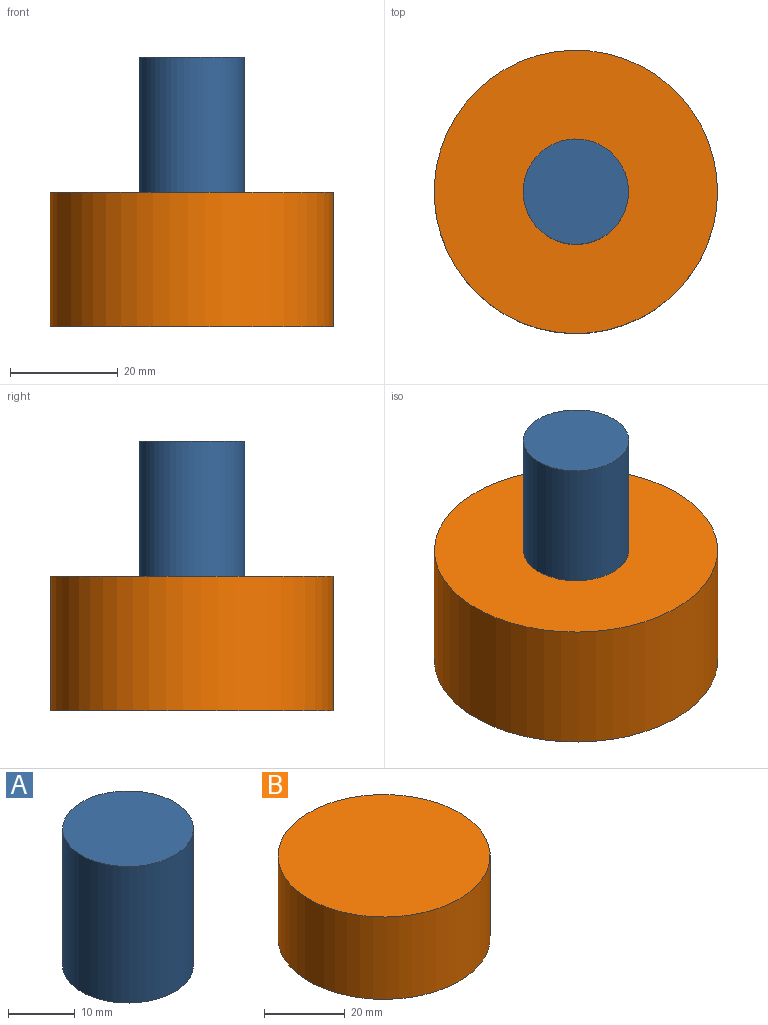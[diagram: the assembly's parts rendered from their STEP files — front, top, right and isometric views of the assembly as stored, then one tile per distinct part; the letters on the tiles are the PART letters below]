
ASSEMBLY  parts=2 mates=1
PART A: 3 faces, bbox 19.6x19.6x25 mm
  f0: cylinder r=9.79mm len=25mm, axis (0,0,-1), area 1537.3mm2, adj f1,f2
  f1: plane 19.57x19.57mm, normal (0,0,1), area 300.9mm2, adj f0
  f2: plane 19.57x19.57mm, normal (0,0,-1), area 300.9mm2, adj f0
PART B: 3 faces, bbox 52.6x52.6x25 mm
  f0: cylinder r=26.31mm len=52.62mm, axis (0,0,-1), area 4132.5mm2, adj f1,f2
  f1: plane 52.62x52.62mm, normal (0,0,1), area 2174.3mm2, adj f0
  f2: plane 52.62x52.62mm, normal (0,0,-1), area 2174.3mm2, adj f0
PLACE A t=(0,0,25)mm
PLACE B at identity
MATE fastened A.f0 <-> B.f0  axis (0,0,1) through (0,0,25)mm
